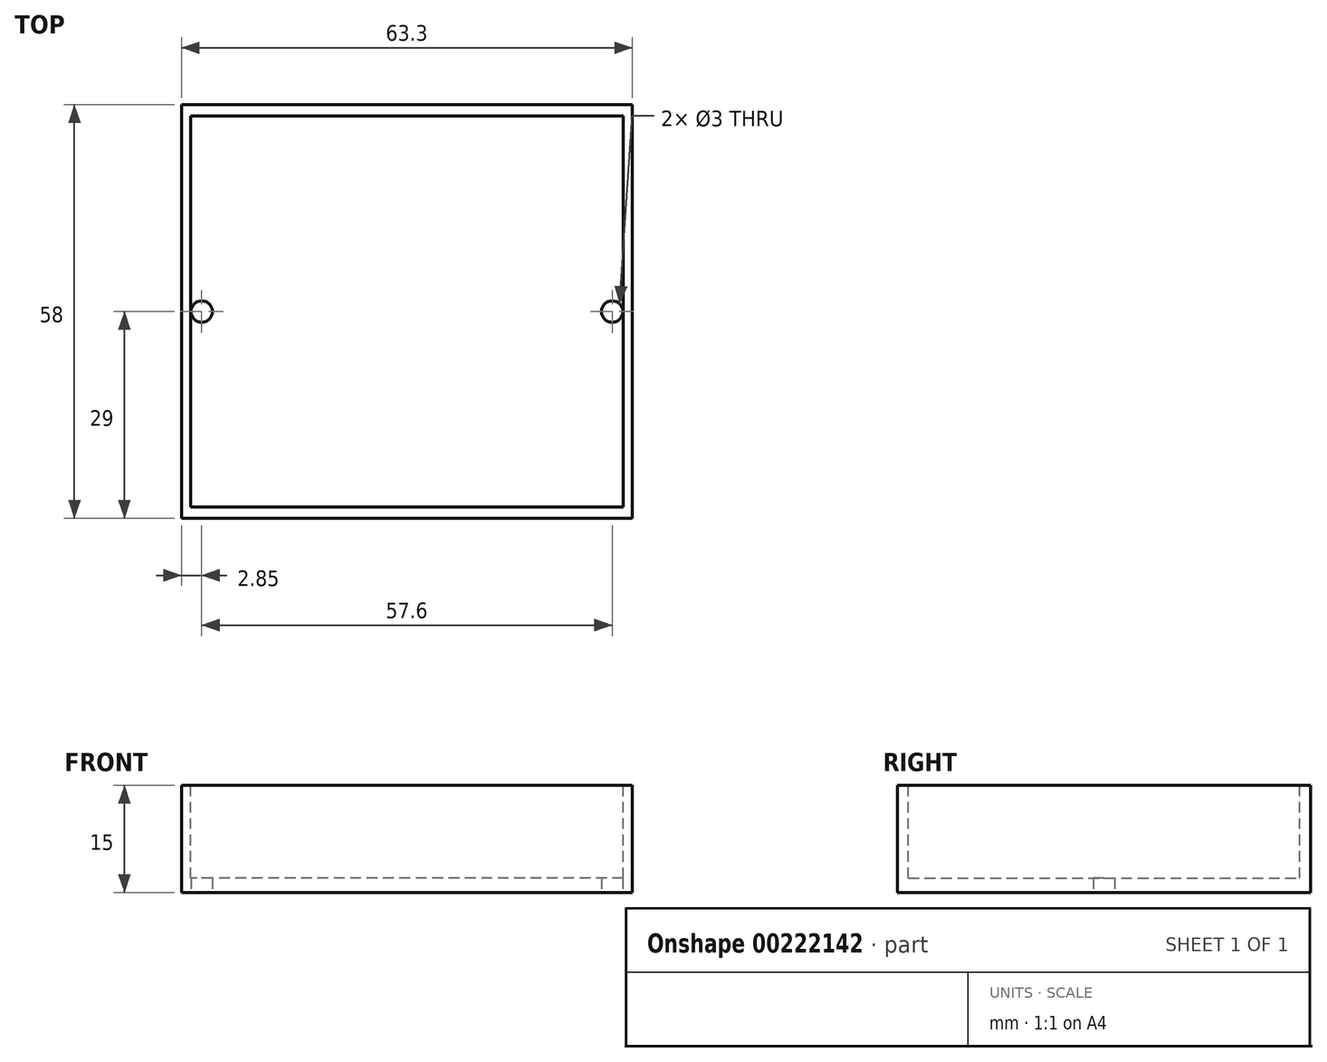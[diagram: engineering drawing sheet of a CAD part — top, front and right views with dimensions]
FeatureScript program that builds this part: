
annotation { "Feature Type Name" : "Feature", "Feature Type Description" : "" }
export const myFeature = defineFeature(function(context is Context, id is Id, definition is map)
    precondition{}
    {
        {
            var Q0;
            Q0=qCreatedBy(makeId("Top.planeOp"),FACE);
            var sketch = newSketch(context, id + "F0", { "sketchPlane" : qUnion([Q0])});
            skLineSegment(sketch, "E0.bottom", {"start": v(31.65, 29) * mm, "end": v(-31.65, 29) * mm});
            skLineSegment(sketch, "E0.top", {"start": v(31.65, -29) * mm, "end": v(-31.65, -29) * mm});
            skLineSegment(sketch, "E0.left", {"start": v(31.65, 29) * mm, "end": v(31.65, -29) * mm});
            skLineSegment(sketch, "E0.right", {"start": v(-31.65, 29) * mm, "end": v(-31.65, -29) * mm});
            skPoint(sketch, "E0.middle", {"position": v(0, 0) * mm});
            skSolve(sketch);
        }
        {
            var Q0;
            Q0 = qSketchRegion(id + "F0", true);
            extrude(context, id + "F1", {"entities" : qUnion([Q0]), "depth" : 15 * mm});
        }
        {
            var Q0;
            Q0=makeQuery(id+"F1.opExtrude","CAP_FACE",FACE,{"disambiguationData":[OSD([sQuery(id+"F0.wireOp",EDGE,"E0.bottom"),sQuery(id+"F0.wireOp",EDGE,"E0.top"),sQuery(id+"F0.wireOp",EDGE,"E0.left"),sQuery(id+"F0.wireOp",EDGE,"E0.right")])],"isStart":false});
            var sketch = newSketch(context, id + "F2", { "sketchPlane" : qUnion([Q0])});
            skLineSegment(sketch, "E1.bottom", {"start": v(30.35, -27.45) * mm, "end": v(-30.35, -27.45) * mm});
            skLineSegment(sketch, "E1.top", {"start": v(30.35, 27.45) * mm, "end": v(-30.35, 27.45) * mm});
            skLineSegment(sketch, "E1.left", {"start": v(30.35, -27.45) * mm, "end": v(30.35, 27.45) * mm});
            skLineSegment(sketch, "E1.right", {"start": v(-30.35, -27.45) * mm, "end": v(-30.35, 27.45) * mm});
            skPoint(sketch, "E1.middle", {"position": v(0, 0) * mm});
            skSolve(sketch);
        }
        {
            var Q0;
            Q0 = qSketchRegion(id + "F2", true);
            extrude(context, id + "F3", {"entities" : qUnion([Q0]), "operationType" : NewBodyOperationType.REMOVE, "oppositeDirection" : true, "depth" : 13 * mm});
        }
        {
            var Q0;
            Q0=makeQuery(id+"F1.opExtrude","CAP_FACE",FACE,{"disambiguationData":[OSD([sQuery(id+"F0.wireOp",EDGE,"E0.bottom"),sQuery(id+"F0.wireOp",EDGE,"E0.top"),sQuery(id+"F0.wireOp",EDGE,"E0.left"),sQuery(id+"F0.wireOp",EDGE,"E0.right")])],"isStart":true});
            var sketch = newSketch(context, id + "F4", { "sketchPlane" : qUnion([Q0])});
            skCircle(sketch, "E2", {"center": v(0, 0) * mm, "radius": 28.8 * mm, "construction": true});
            skCircle(sketch, "E3", {"center": v(28.8, 0) * mm, "radius": 1.5 * mm});
            skPoint(sketch, "E3.centerSnap0", {"position": v(31.65, 0) * mm});
            skCircle(sketch, "E4", {"center": v(-28.8, 0) * mm, "radius": 1.5 * mm});
            skSolve(sketch);
        }
        {
            var Q0;
            Q0 = qSketchRegion(id + "F4", true);
            extrude(context, id + "F5", {"entities" : qUnion([Q0]), "operationType" : NewBodyOperationType.REMOVE, "endBound" : BoundingType.THROUGH_ALL, "oppositeDirection" : true, "depth" : 25 * mm});
        }
    });
